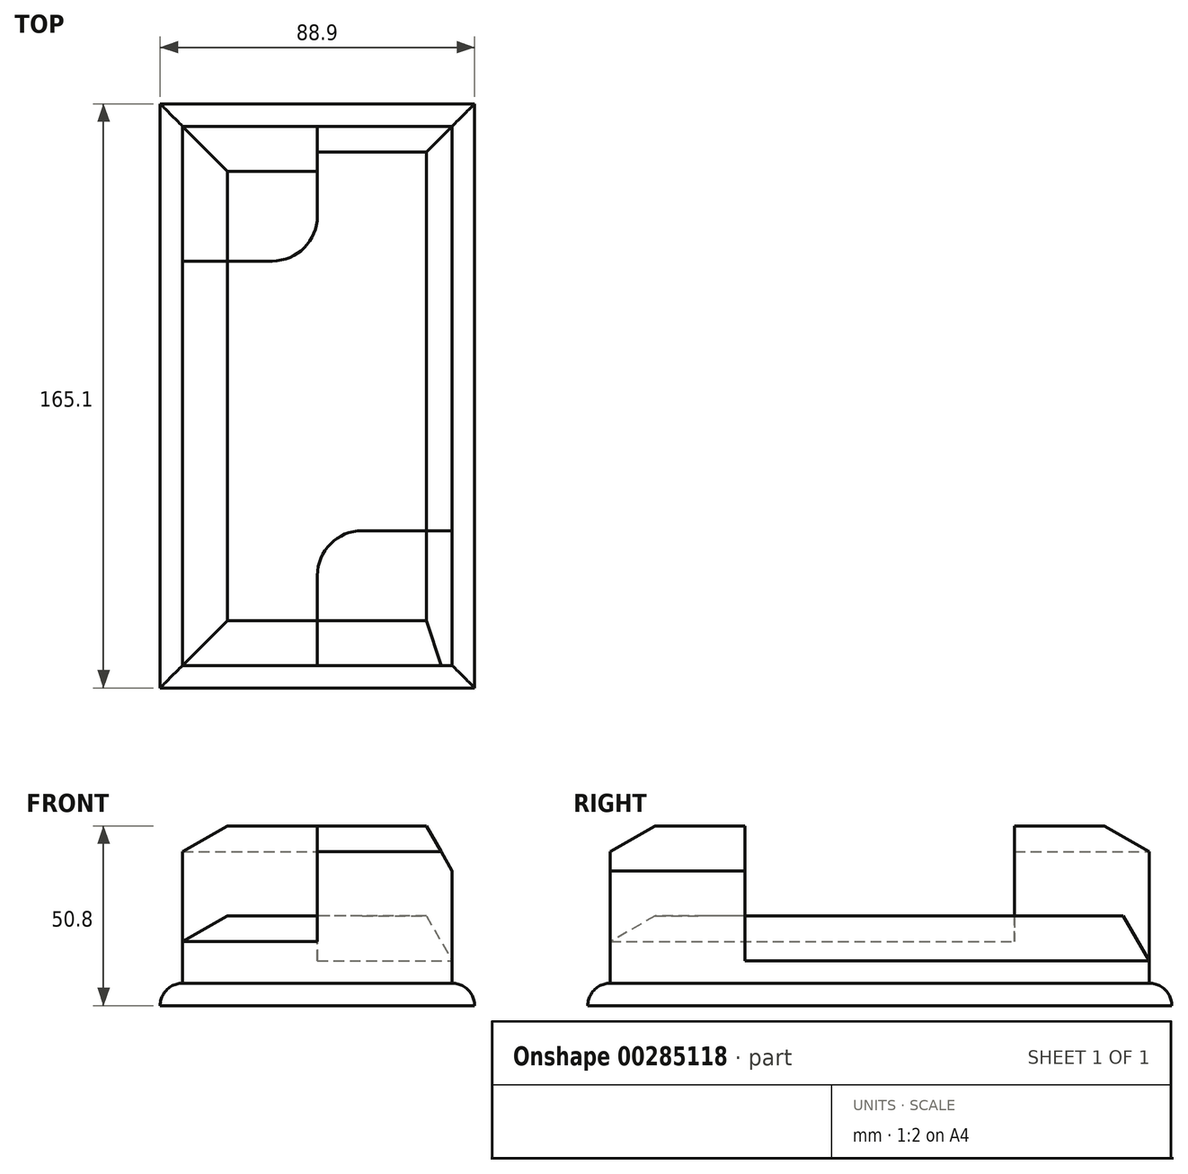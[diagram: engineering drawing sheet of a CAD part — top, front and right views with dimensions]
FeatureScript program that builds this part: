
annotation { "Feature Type Name" : "Feature", "Feature Type Description" : "" }
export const myFeature = defineFeature(function(context is Context, id is Id, definition is map)
    precondition{}
    {
        {
            var Q0;
            Q0=qCreatedBy(makeId("Top.planeOp"),FACE);
            var sketch = newSketch(context, id + "F0", { "sketchPlane" : qUnion([Q0])});
            skLineSegment(sketch, "E0.bottom", {"start": v(-99.09, 77.1) * mm, "end": v(-10.19, 77.1) * mm});
            skLineSegment(sketch, "E0.top", {"start": v(-99.09, -88) * mm, "end": v(-10.19, -88) * mm});
            skLineSegment(sketch, "E0.left", {"start": v(-99.09, 77.1) * mm, "end": v(-99.09, -88) * mm});
            skLineSegment(sketch, "E0.right", {"start": v(-10.19, 77.1) * mm, "end": v(-10.19, -88) * mm});
            skLineSegment(sketch, "E1.0", {"start": v(-92.74, 70.74) * mm, "end": v(-16.54, 70.74) * mm});
            skLineSegment(sketch, "E1.1", {"start": v(-92.74, 70.74) * mm, "end": v(-92.74, -81.66) * mm});
            skLineSegment(sketch, "E1.2", {"start": v(-92.74, -81.66) * mm, "end": v(-16.54, -81.66) * mm});
            skLineSegment(sketch, "E1.3", {"start": v(-16.54, 70.74) * mm, "end": v(-16.54, -81.66) * mm});
            skLineSegment(sketch, "E2", {"start": v(-54.64, 70.74) * mm, "end": v(-54.64, 45.34) * mm});
            skLineSegment(sketch, "E3", {"start": v(-67.34, 32.64) * mm, "end": v(-92.74, 32.64) * mm});
            skLineSegment(sketch, "E4", {"start": v(-54.64, -81.66) * mm, "end": v(-54.64, -56.26) * mm});
            skLineSegment(sketch, "E5", {"start": v(-41.94, -43.56) * mm, "end": v(-16.54, -43.56) * mm});
            skPoint(sketch, "E6.visualSharp", {"position": v(-54.64, 32.64) * mm});
            skArc(sketch, "E6.filletArc", {"start": v(-67.34, 32.64) * mm, "mid": v(-58.36, 36.36) * mm, "end": v(-54.64, 45.34) * mm});
            skPoint(sketch, "E7.visualSharp", {"position": v(-54.64, -43.56) * mm});
            skArc(sketch, "E7.filletArc", {"start": v(-41.94, -43.56) * mm, "mid": v(-50.92, -47.28) * mm, "end": v(-54.64, -56.26) * mm});
            skSolve(sketch);
        }
        {
            var Q0;
            Q0=makeQuery(id+"F0.imprint","IMPRINT",FACE,{"disambiguationData":[TD([[makeQuery(id+"F0.imprint","IMPRINT",EDGE,{"derivedFrom":sQuery(id+"F0.wireOp",EDGE,"E0.bottom")}),-1.0]])]});
            extrude(context, id + "F1", {"entities" : qUnion([Q0]), "depth" : 6.35 * mm});
        }
        {
            var Q0;
            {var subQ9=sQuery(id+"F0.wireOp",EDGE,"E2");Q0=makeQuery(id+"F0.imprint","IMPRINT",FACE,{"disambiguationData":[TD([[makeQuery(id+"F0.imprint","IMPRINT",EDGE,{"derivedFrom":subQ9}),1.0]])]});}
            extrude(context, id + "F2", {"entities" : qUnion([Q0]), "operationType" : NewBodyOperationType.ADD, "depth" : 25.4 * mm});
        }
        {
            var Q0;
            {var subQ1=sQuery(id+"F0.wireOp",EDGE,"E2");Q0=makeQuery(id+"F0.imprint","IMPRINT",FACE,{"disambiguationData":[TD([[makeQuery(id+"F0.imprint","IMPRINT",EDGE,{"derivedFrom":subQ1}),-1.0]])]});}
            var Q1;
            {var subQ4=sQuery(id+"F0.wireOp",EDGE,"E4");Q1=makeQuery(id+"F0.imprint","IMPRINT",FACE,{"disambiguationData":[TD([[makeQuery(id+"F0.imprint","IMPRINT",EDGE,{"derivedFrom":subQ4}),-1.0]])]});}
            extrude(context, id + "F3", {"entities" : qUnion([Q0, Q1]), "operationType" : NewBodyOperationType.ADD, "depth" : 50.8 * mm});
        }
        {
            var Q0;
            Q0=makeQuery(id+"F1.opExtrude","CAP_EDGE",EDGE,{"disambiguationData":[OSD([sQuery(id+"F0.wireOp",EDGE,"E0.left")])],"isStart":false});
            var Q1;
            Q1=makeQuery(id+"F1.opExtrude","CAP_EDGE",EDGE,{"disambiguationData":[OSD([sQuery(id+"F0.wireOp",EDGE,"E0.top")])],"isStart":false});
            var Q2;
            Q2=makeQuery(id+"F1.opExtrude","CAP_EDGE",EDGE,{"disambiguationData":[OSD([sQuery(id+"F0.wireOp",EDGE,"E0.right")])],"isStart":false});
            var Q3;
            Q3=makeQuery(id+"F1.opExtrude","CAP_EDGE",EDGE,{"disambiguationData":[OSD([sQuery(id+"F0.wireOp",EDGE,"E0.bottom")])],"isStart":false});
            fillet(context, id + "F4", {"entities" : qUnion([Q0, Q1, Q2, Q3]), "radius" : 6.35 * mm, "tangentPropagation" : true, "allowEdgeOverflow" : false});
        }
        {
            var Q0;
            Q0=makeQuery(id+"F3.opExtrude","CAP_EDGE",EDGE,{"disambiguationData":[OSD([sQuery(id+"F0.wireOp",EDGE,"E1.1")])],"isStart":false});
            var Q1;
            Q1=makeQuery(id+"F3.opExtrude","CAP_EDGE",EDGE,{"disambiguationData":[OSD([sQuery(id+"F0.wireOp",EDGE,"E1.0")])],"isStart":false});
            var Q2;
            Q2=makeQuery(id+"F3.opExtrude","CAP_EDGE",EDGE,{"disambiguationData":[OSD([sQuery(id+"F0.wireOp",EDGE,"E1.2")])],"isStart":false});
            var Q3;
            Q3=makeQuery(id+"F3.opExtrude","CAP_EDGE",EDGE,{"disambiguationData":[OSD([sQuery(id+"F0.wireOp",EDGE,"E1.3")])],"isStart":false});
            var Q4;
            Q4=makeQuery(id+"F2.opExtrude","CAP_EDGE",EDGE,{"disambiguationData":[OSD([sQuery(id+"F0.wireOp",EDGE,"E1.2")])],"isStart":false});
            var Q5;
            Q5=makeQuery(id+"F2.opExtrude","CAP_EDGE",EDGE,{"disambiguationData":[OSD([sQuery(id+"F0.wireOp",EDGE,"E1.1")])],"isStart":false});
            var Q6;
            Q6=makeQuery(id+"F2.opExtrude","CAP_EDGE",EDGE,{"disambiguationData":[OSD([sQuery(id+"F0.wireOp",EDGE,"E1.3")])],"isStart":false});
            var Q7;
            Q7=makeQuery(id+"F2.opExtrude","CAP_EDGE",EDGE,{"disambiguationData":[OSD([sQuery(id+"F0.wireOp",EDGE,"E1.0")])],"isStart":false});
            chamfer(context, id + "F5", {"entities" : qUnion([Q0, Q1, Q2, Q3, Q4, Q5, Q6, Q7]), "chamferType" : ChamferType.OFFSET_ANGLE, "width" : 12.7 * mm, "oppositeDirection" : false, "angle" : 30 * degree, "tangentPropagation" : true});
        }
    });
